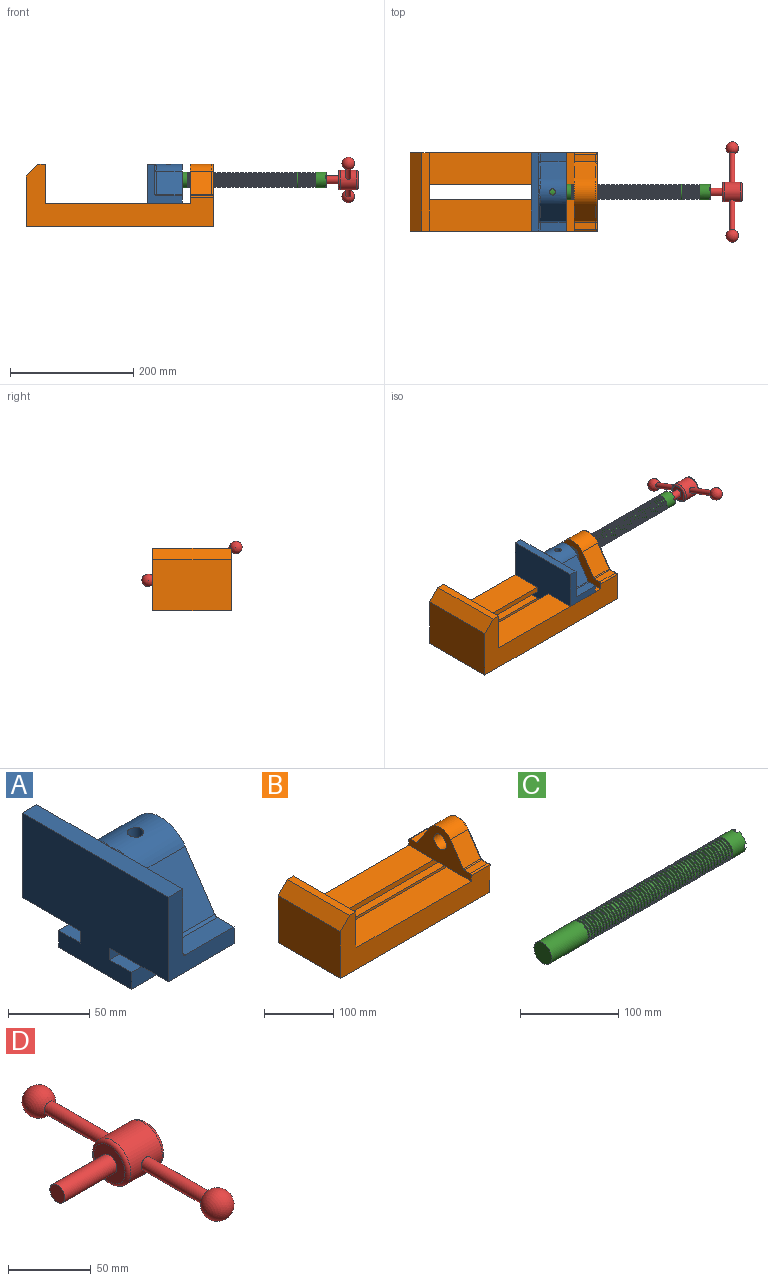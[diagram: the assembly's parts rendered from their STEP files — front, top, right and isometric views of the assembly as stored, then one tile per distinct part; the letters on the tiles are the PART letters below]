
ASSEMBLY  parts=4 mates=3
PART A: 36 faces, bbox 57.2x127x89 mm
  f0: plane 57.15x50.8mm, normal (0,0,-1), area 2903.2mm2, adj f6,f9,f10,f23
  f1: cylinder r=12.7mm len=44.45mm, axis (1,0,0), area 3464.3mm2, adj f6,f15,f16
  f2: plane 41.91x14.52mm, normal (0,0,1), area 608.5mm2, adj f6,f11,f24,f25
  f3: plane 51.86x48.26mm, normal (1,0,0), area 1495.7mm2, adj f8,f10,f31,f33,f35
  f4: plane 51.86x48.26mm, normal (1,0,0), area 1495.7mm2, adj f8,f11,f24,f28,f29
  f5: plane 57.15x50.8mm, normal (0,0,-1), area 2903.2mm2, adj f6,f9,f11,f22
  f6: plane 127x85.09mm, normal (1,0,0), area 5190.6mm2, adj f0,f1,f2,f5,f7,f10,f11,f12
  f7: plane 41.91x14.52mm, normal (0,0,1), area 608.5mm2, adj f6,f10,f30,f31
  f8: plane 127x12.7mm, normal (0,0,1), area 1612.9mm2, adj f3,f4,f9,f10,f11,f26,f34
  f9: plane 127x85.09mm, normal (-1,0,0), area 9096.8mm2, adj f0,f5,f8,f10,f11,f17,f18,f19
  f10: plane 63.5x57.15mm, normal (0,-1,0), area 1372.3mm2, adj f0,f3,f6,f7,f8,f9,f31
  f11: plane 63.5x57.15mm, normal (0,1,0), area 1372.3mm2, adj f2,f4,f5,f6,f8,f9,f24
  f12: plane 41.91x38.43mm, normal (0,-0.83,0.56), area 1939.2mm2, adj f6,f13,f30,f33
  f13: cylinder r=25.4mm len=44.45mm, axis (1,0,0), area 2026.5mm2, adj f6,f12,f14,f16,f26,f28,f34,f35
  f14: plane 41.91x38.43mm, normal (0,0.83,0.56), area 1939.2mm2, adj f6,f13,f25,f29
  f15: plane 25.4x25.4mm, normal (1,0,0), area 506.7mm2, adj f1
  f16: cylinder r=5.08mm len=13.76mm, axis (0,0,1), area 414mm2, adj f1,f13
  f17: plane 57.15x19.05mm, normal (0,0,1), area 1088.7mm2, adj f6,f9,f18,f23
  f18: plane 57.15x12.7mm, normal (0,-1,0), area 725.8mm2, adj f6,f9,f17,f19
  f19: plane 63.5x57.15mm, normal (0,0,-1), area 3629mm2, adj f6,f9,f18,f20
  f20: plane 57.15x12.7mm, normal (0,1,0), area 725.8mm2, adj f6,f9,f19,f21
  f21: plane 57.15x19.05mm, normal (0,0,1), area 1088.7mm2, adj f6,f9,f20,f22
  f22: plane 57.15x8.89mm, normal (0,1,0), area 508.1mm2, adj f5,f6,f9,f21
  f23: plane 57.15x8.89mm, normal (0,-1,0), area 508.1mm2, adj f0,f6,f9,f17
  f24: cylinder r=2.54mm len=14.52mm, axis (0,-1,0), area 57.9mm2, adj f2,f4,f11,f27
  f25: cylinder r=2.54mm len=41.91mm, axis (1,0,0), area 104.3mm2, adj f2,f6,f14,f27
  f26: bspline ~12.24x2.8mm, area 20.9mm2, adj f8,f13,f28
  f27: sphere r=2.54mm, area 6.3mm2, adj f24,f25,f29
  f28: torus R=27.94mm, axis (1,0,0), area 57.8mm2, adj f4,f13,f26,f29
  f29: cylinder r=2.54mm len=39.84mm, axis (0,-0.56,0.83), area 184.6mm2, adj f4,f14,f27,f28
  f30: cylinder r=2.54mm len=41.91mm, axis (1,0,0), area 104.3mm2, adj f6,f7,f12,f32
  f31: cylinder r=2.54mm len=14.52mm, axis (0,-1,0), area 57.9mm2, adj f3,f7,f10,f32
  f32: sphere r=2.54mm, area 6.3mm2, adj f30,f31,f33
  f33: cylinder r=2.54mm len=39.84mm, axis (0,-0.56,-0.83), area 184.6mm2, adj f3,f12,f32,f35
  f34: bspline ~12.24x2.8mm, area 20.9mm2, adj f8,f13,f35
  f35: torus R=27.94mm, axis (1,0,0), area 57.8mm2, adj f3,f13,f33,f34
PART B: 39 faces, bbox 304.8x127x103.7 mm
  f0: plane 234.95x50.8mm, normal (0,0,1), area 11935.5mm2, adj f2,f8,f16,f26
  f1: plane 234.95x50.8mm, normal (0,0,1), area 11935.5mm2, adj f2,f9,f16,f27
  f2: plane 127x101.6mm, normal (1,0,0), area 9516.1mm2, adj f0,f1,f3,f6,f8,f9,f18,f19
  f3: plane 127x12.7mm, normal (0,0,1), area 1612.9mm2, adj f2,f4,f8,f9
  f4: plane 127x19.05mm, normal (-0.71,0,0.71), area 3421.5mm2, adj f3,f5,f8,f9
  f5: plane 127x82.55mm, normal (-1,0,0), area 10483.9mm2, adj f4,f6,f8,f9
  f6: plane 304.8x127mm, normal (0,0,-1), area 31774.1mm2, adj f2,f5,f7,f8,f9,f21,f22
  f7: plane 127x99.06mm, normal (1,0,0), area 7097.5mm2, adj f6,f8,f9,f14,f17,f18,f19,f20
  f8: plane 304.8x101.6mm, normal (0,-1,0), area 13834.6mm2, adj f0,f2,f3,f4,f5,f6,f7,f16
  f9: plane 304.8x101.6mm, normal (0,1,0), area 13834.6mm2, adj f1,f2,f3,f4,f5,f6,f7,f16
  f10: plane 35.56x11.98mm, normal (0,0,1), area 426mm2, adj f16,f28,f29,f30
  f11: plane 38.43x35.56mm, normal (0,0.83,0.56), area 1645.4mm2, adj f12,f16,f29,f32
  f12: cylinder r=25.4mm len=42.19mm, axis (1,0,0), area 1770.2mm2, adj f11,f13,f16,f33
  f13: plane 38.43x35.56mm, normal (0,-0.83,0.56), area 1645.4mm2, adj f12,f16,f34,f35
  f14: cylinder r=12.7mm len=38.1mm, axis (1,0,0), area 3040.2mm2, adj f7,f16
  f15: plane 35.56x11.98mm, normal (0,0,1), area 426mm2, adj f16,f34,f36,f38
  f16: plane 127x63.5mm, normal (-1,0,0), area 4155.5mm2, adj f0,f1,f8,f9,f10,f11,f12,f13
  f17: plane 38.1x25.4mm, normal (0,0,-1), area 967.7mm2, adj f7,f16,f26,f27
  f18: plane 273.05x19.05mm, normal (0,0,-1), area 5201.6mm2, adj f2,f7,f19,f26
  f19: plane 273.05x12.7mm, normal (0,1,0), area 3467.7mm2, adj f2,f7,f18,f20
  f20: plane 273.05x19.05mm, normal (0,0,1), area 5201.6mm2, adj f2,f7,f19,f21
  f21: plane 273.05x16.51mm, normal (0,1,0), area 4508.1mm2, adj f2,f6,f7,f20
  f22: plane 273.05x16.51mm, normal (0,-1,0), area 4508.1mm2, adj f2,f6,f7,f23
  f23: plane 273.05x19.05mm, normal (0,0,1), area 5201.6mm2, adj f2,f7,f22,f24
  f24: plane 273.05x12.7mm, normal (0,-1,0), area 3467.7mm2, adj f2,f7,f23,f25
  f25: plane 273.05x19.05mm, normal (0,0,-1), area 5201.6mm2, adj f2,f7,f24,f27
  f26: plane 273.05x8.89mm, normal (0,1,0), area 2427.4mm2, adj f0,f2,f7,f17,f18
  f27: plane 273.05x8.89mm, normal (0,-1,0), area 2427.4mm2, adj f1,f2,f7,f17,f25
  f28: cylinder r=2.54mm len=38.1mm, axis (1,0,0), area 148.3mm2, adj f9,f10,f16,f30
  f29: cylinder r=2.54mm len=35.56mm, axis (-1,0,0), area 88.5mm2, adj f10,f11,f16,f31
  f30: cylinder r=2.54mm len=14.52mm, axis (0,1,0), area 54.3mm2, adj f7,f10,f28,f31
  f31: torus R=5.08mm, axis (-1,0,0), area 13.5mm2, adj f7,f29,f30,f32
  f32: cylinder r=2.54mm len=39.84mm, axis (0,0.56,-0.83), area 184.6mm2, adj f7,f11,f31,f33
  f33: torus R=22.86mm, axis (-1,0,0), area 191.4mm2, adj f7,f12,f32,f35
  f34: cylinder r=2.54mm len=35.56mm, axis (-1,0,0), area 88.5mm2, adj f13,f15,f16,f37
  f35: cylinder r=2.54mm len=39.84mm, axis (0,0.56,0.83), area 184.6mm2, adj f7,f13,f33,f37
  f36: cylinder r=2.54mm len=38.1mm, axis (-1,0,0), area 148.3mm2, adj f8,f15,f16,f38
  f37: torus R=5.08mm, axis (-1,0,0), area 13.5mm2, adj f7,f34,f35,f38
  f38: cylinder r=2.54mm len=14.52mm, axis (0,1,0), area 54.3mm2, adj f7,f15,f36,f37
PART C: 220 faces, bbox 279.4x25.4x25.4 mm
  f0: cylinder r=12.7mm len=25.4mm, axis (-1,0,0), area 1468.2mm2, adj f1,f2,f3,f5,f7,f208,f209,f210
  f1: plane 9.9x9.9mm, normal (1,0,0), area 62.3mm2, adj f0,f4,f213,f216
  f2: plane 9.9x9.9mm, normal (1,0,0), area 62.3mm2, adj f0,f4,f210,f218
  f3: plane 9.9x9.9mm, normal (1,0,0), area 62.3mm2, adj f0,f4,f209,f212
  f4: cylinder r=6.35mm len=25.4mm, axis (1,0,0), area 960.3mm2, adj f1,f2,f3,f5,f6,f208,f209,f210
  f5: plane 9.9x9.9mm, normal (1,0,0), area 62.3mm2, adj f0,f4,f215,f217
  f6: plane 12.7x12.7mm, normal (1,0,0), area 126.7mm2, adj f4
  f7: cone r=12.7mm half-angle=76deg, axis (1,0,0), area 188mm2, adj f0,f9
  f8: cone r=10.16mm half-angle=76deg, axis (-1,0,0), area 188mm2, adj f9,f10
  f9: cylinder r=10.16mm len=20.32mm, axis (1,0,0), area 81.1mm2, adj f7,f8
  f10: cylinder r=12.7mm len=25.4mm, axis (-1,0,0), area 131.7mm2, adj f8,f11
  f11: cone r=12.7mm half-angle=76deg, axis (1,0,0), area 188mm2, adj f10,f13
  f12: cone r=10.16mm half-angle=76deg, axis (-1,0,0), area 188mm2, adj f13,f14
  f13: cylinder r=10.16mm len=20.32mm, axis (1,0,0), area 81.1mm2, adj f11,f12
  f14: cylinder r=12.7mm len=25.4mm, axis (-1,0,0), area 131.7mm2, adj f12,f15
  f15: cone r=12.7mm half-angle=76deg, axis (1,0,0), area 188mm2, adj f14,f17
  f16: cone r=10.16mm half-angle=76deg, axis (-1,0,0), area 188mm2, adj f17,f18
  f17: cylinder r=10.16mm len=20.32mm, axis (1,0,0), area 81.1mm2, adj f15,f16
  f18: cylinder r=12.7mm len=25.4mm, axis (-1,0,0), area 131.7mm2, adj f16,f19
  f19: cone r=12.7mm half-angle=76deg, axis (1,0,0), area 188mm2, adj f18,f21
  f20: cone r=10.16mm half-angle=76deg, axis (-1,0,0), area 188mm2, adj f21,f22
  f21: cylinder r=10.16mm len=20.32mm, axis (1,0,0), area 81.1mm2, adj f19,f20
  f22: cylinder r=12.7mm len=25.4mm, axis (-1,0,0), area 131.7mm2, adj f20,f23
  f23: cone r=12.7mm half-angle=76deg, axis (1,0,0), area 188mm2, adj f22,f25
  f24: cone r=10.16mm half-angle=76deg, axis (-1,0,0), area 188mm2, adj f25,f26
  f25: cylinder r=10.16mm len=20.32mm, axis (1,0,0), area 81.1mm2, adj f23,f24
  f26: cylinder r=12.7mm len=25.4mm, axis (-1,0,0), area 131.7mm2, adj f24,f27
  f27: cone r=12.7mm half-angle=76deg, axis (1,0,0), area 188mm2, adj f26,f29
  f28: cone r=10.16mm half-angle=76deg, axis (-1,0,0), area 188mm2, adj f29,f30
  f29: cylinder r=10.16mm len=20.32mm, axis (1,0,0), area 81.1mm2, adj f27,f28
  f30: cylinder r=12.7mm len=25.4mm, axis (-1,0,0), area 131.7mm2, adj f28,f31
  f31: cone r=12.7mm half-angle=76deg, axis (1,0,0), area 188mm2, adj f30,f33
  f32: cone r=10.16mm half-angle=76deg, axis (-1,0,0), area 188mm2, adj f33,f34
  f33: cylinder r=10.16mm len=20.32mm, axis (1,0,0), area 81.1mm2, adj f31,f32
  f34: cylinder r=12.7mm len=25.4mm, axis (-1,0,0), area 131.7mm2, adj f32,f35
  f35: cone r=12.7mm half-angle=76deg, axis (1,0,0), area 188mm2, adj f34,f37
  f36: cone r=10.16mm half-angle=76deg, axis (-1,0,0), area 188mm2, adj f37,f38
  f37: cylinder r=10.16mm len=20.32mm, axis (1,0,0), area 81.1mm2, adj f35,f36
  f38: cylinder r=12.7mm len=25.4mm, axis (-1,0,0), area 131.7mm2, adj f36,f39
  f39: cone r=12.7mm half-angle=76deg, axis (1,0,0), area 188mm2, adj f38,f41
  f40: cone r=10.16mm half-angle=76deg, axis (-1,0,0), area 188mm2, adj f41,f42
  f41: cylinder r=10.16mm len=20.32mm, axis (1,0,0), area 81.1mm2, adj f39,f40
  f42: cylinder r=12.7mm len=25.4mm, axis (-1,0,0), area 131.7mm2, adj f40,f43
  f43: cone r=12.7mm half-angle=76deg, axis (1,0,0), area 188mm2, adj f42,f45
  f44: cone r=10.16mm half-angle=76deg, axis (-1,0,0), area 188mm2, adj f45,f46
  f45: cylinder r=10.16mm len=20.32mm, axis (1,0,0), area 81.1mm2, adj f43,f44
  f46: cylinder r=12.7mm len=25.4mm, axis (-1,0,0), area 131.7mm2, adj f44,f47
  f47: cone r=12.7mm half-angle=76deg, axis (1,0,0), area 188mm2, adj f46,f49
  f48: cone r=10.16mm half-angle=76deg, axis (-1,0,0), area 188mm2, adj f49,f50
  f49: cylinder r=10.16mm len=20.32mm, axis (1,0,0), area 81.1mm2, adj f47,f48
  f50: cylinder r=12.7mm len=25.4mm, axis (-1,0,0), area 131.7mm2, adj f48,f51
  f51: cone r=12.7mm half-angle=76deg, axis (1,0,0), area 188mm2, adj f50,f53
  f52: cone r=10.16mm half-angle=76deg, axis (-1,0,0), area 188mm2, adj f53,f54
  f53: cylinder r=10.16mm len=20.32mm, axis (1,0,0), area 81.1mm2, adj f51,f52
  f54: cylinder r=12.7mm len=25.4mm, axis (-1,0,0), area 131.7mm2, adj f52,f55
  f55: cone r=12.7mm half-angle=76deg, axis (1,0,0), area 188mm2, adj f54,f57
  f56: cone r=10.16mm half-angle=76deg, axis (-1,0,0), area 188mm2, adj f57,f58
  f57: cylinder r=10.16mm len=20.32mm, axis (1,0,0), area 81.1mm2, adj f55,f56
  f58: cylinder r=12.7mm len=25.4mm, axis (-1,0,0), area 131.7mm2, adj f56,f59
  f59: cone r=12.7mm half-angle=76deg, axis (1,0,0), area 188mm2, adj f58,f61
  f60: cone r=10.16mm half-angle=76deg, axis (-1,0,0), area 188mm2, adj f61,f62
  f61: cylinder r=10.16mm len=20.32mm, axis (1,0,0), area 81.1mm2, adj f59,f60
  f62: cylinder r=12.7mm len=25.4mm, axis (-1,0,0), area 131.7mm2, adj f60,f63
  f63: cone r=12.7mm half-angle=76deg, axis (1,0,0), area 188mm2, adj f62,f65
  f64: cone r=10.16mm half-angle=76deg, axis (-1,0,0), area 188mm2, adj f65,f66
  f65: cylinder r=10.16mm len=20.32mm, axis (1,0,0), area 81.1mm2, adj f63,f64
  f66: cylinder r=12.7mm len=25.4mm, axis (-1,0,0), area 131.7mm2, adj f64,f67
  f67: cone r=12.7mm half-angle=76deg, axis (1,0,0), area 188mm2, adj f66,f69
  f68: cone r=10.16mm half-angle=76deg, axis (-1,0,0), area 188mm2, adj f69,f70
  f69: cylinder r=10.16mm len=20.32mm, axis (1,0,0), area 81.1mm2, adj f67,f68
  f70: cylinder r=12.7mm len=25.4mm, axis (-1,0,0), area 131.7mm2, adj f68,f71
  f71: cone r=12.7mm half-angle=76deg, axis (1,0,0), area 188mm2, adj f70,f73
  f72: cone r=10.16mm half-angle=76deg, axis (-1,0,0), area 188mm2, adj f73,f74
  f73: cylinder r=10.16mm len=20.32mm, axis (1,0,0), area 81.1mm2, adj f71,f72
  f74: cylinder r=12.7mm len=25.4mm, axis (-1,0,0), area 131.7mm2, adj f72,f75
  f75: cone r=12.7mm half-angle=76deg, axis (1,0,0), area 188mm2, adj f74,f77
  f76: cone r=10.16mm half-angle=76deg, axis (-1,0,0), area 188mm2, adj f77,f78
  f77: cylinder r=10.16mm len=20.32mm, axis (1,0,0), area 81.1mm2, adj f75,f76
  f78: cylinder r=12.7mm len=25.4mm, axis (-1,0,0), area 131.7mm2, adj f76,f79
  f79: cone r=12.7mm half-angle=76deg, axis (1,0,0), area 188mm2, adj f78,f81
  f80: cone r=10.16mm half-angle=76deg, axis (-1,0,0), area 188mm2, adj f81,f82
  f81: cylinder r=10.16mm len=20.32mm, axis (1,0,0), area 81.1mm2, adj f79,f80
  f82: cylinder r=12.7mm len=25.4mm, axis (-1,0,0), area 131.7mm2, adj f80,f83
  f83: cone r=12.7mm half-angle=76deg, axis (1,0,0), area 188mm2, adj f82,f85
  f84: cone r=10.16mm half-angle=76deg, axis (-1,0,0), area 188mm2, adj f85,f86
  f85: cylinder r=10.16mm len=20.32mm, axis (1,0,0), area 81.1mm2, adj f83,f84
  f86: cylinder r=12.7mm len=25.4mm, axis (-1,0,0), area 131.7mm2, adj f84,f87
  f87: cone r=12.7mm half-angle=76deg, axis (1,0,0), area 188mm2, adj f86,f89
  f88: cone r=10.16mm half-angle=76deg, axis (-1,0,0), area 188mm2, adj f89,f90
  f89: cylinder r=10.16mm len=20.32mm, axis (1,0,0), area 81.1mm2, adj f87,f88
  f90: cylinder r=12.7mm len=25.4mm, axis (-1,0,0), area 131.7mm2, adj f88,f91
  f91: cone r=12.7mm half-angle=76deg, axis (1,0,0), area 188mm2, adj f90,f93
  f92: cone r=10.16mm half-angle=76deg, axis (-1,0,0), area 188mm2, adj f93,f94
  f93: cylinder r=10.16mm len=20.32mm, axis (1,0,0), area 81.1mm2, adj f91,f92
  f94: cylinder r=12.7mm len=25.4mm, axis (-1,0,0), area 131.7mm2, adj f92,f95
  f95: cone r=12.7mm half-angle=76deg, axis (1,0,0), area 188mm2, adj f94,f97
  f96: cone r=10.16mm half-angle=76deg, axis (-1,0,0), area 188mm2, adj f97,f98
  f97: cylinder r=10.16mm len=20.32mm, axis (1,0,0), area 81.1mm2, adj f95,f96
  f98: cylinder r=12.7mm len=25.4mm, axis (-1,0,0), area 131.7mm2, adj f96,f99
  f99: cone r=12.7mm half-angle=76deg, axis (1,0,0), area 188mm2, adj f98,f101
  f100: cone r=10.16mm half-angle=76deg, axis (-1,0,0), area 188mm2, adj f101,f102
  f101: cylinder r=10.16mm len=20.32mm, axis (1,0,0), area 81.1mm2, adj f99,f100
  f102: cylinder r=12.7mm len=25.4mm, axis (-1,0,0), area 131.7mm2, adj f100,f103
  f103: cone r=12.7mm half-angle=76deg, axis (1,0,0), area 188mm2, adj f102,f105
  f104: cone r=10.16mm half-angle=76deg, axis (-1,0,0), area 188mm2, adj f105,f106
  f105: cylinder r=10.16mm len=20.32mm, axis (1,0,0), area 81.1mm2, adj f103,f104
  f106: cylinder r=12.7mm len=25.4mm, axis (-1,0,0), area 131.7mm2, adj f104,f107
  f107: cone r=12.7mm half-angle=76deg, axis (1,0,0), area 188mm2, adj f106,f109
  f108: cone r=10.16mm half-angle=76deg, axis (-1,0,0), area 188mm2, adj f109,f110
  f109: cylinder r=10.16mm len=20.32mm, axis (1,0,0), area 81.1mm2, adj f107,f108
  f110: cylinder r=12.7mm len=25.4mm, axis (-1,0,0), area 131.7mm2, adj f108,f111
  f111: cone r=12.7mm half-angle=76deg, axis (1,0,0), area 188mm2, adj f110,f113
  f112: cone r=10.16mm half-angle=76deg, axis (-1,0,0), area 188mm2, adj f113,f114
  f113: cylinder r=10.16mm len=20.32mm, axis (1,0,0), area 81.1mm2, adj f111,f112
  f114: cylinder r=12.7mm len=25.4mm, axis (-1,0,0), area 131.7mm2, adj f112,f115
  f115: cone r=12.7mm half-angle=76deg, axis (1,0,0), area 188mm2, adj f114,f117
  f116: cone r=10.16mm half-angle=76deg, axis (-1,0,0), area 188mm2, adj f117,f118
  f117: cylinder r=10.16mm len=20.32mm, axis (1,0,0), area 81.1mm2, adj f115,f116
  f118: cylinder r=12.7mm len=25.4mm, axis (-1,0,0), area 131.7mm2, adj f116,f119
  f119: cone r=12.7mm half-angle=76deg, axis (1,0,0), area 188mm2, adj f118,f121
  f120: cone r=10.16mm half-angle=76deg, axis (-1,0,0), area 188mm2, adj f121,f122
  f121: cylinder r=10.16mm len=20.32mm, axis (1,0,0), area 81.1mm2, adj f119,f120
  f122: cylinder r=12.7mm len=25.4mm, axis (-1,0,0), area 131.7mm2, adj f120,f123
  f123: cone r=12.7mm half-angle=76deg, axis (1,0,0), area 188mm2, adj f122,f125
  f124: cone r=10.16mm half-angle=76deg, axis (-1,0,0), area 188mm2, adj f125,f126
  f125: cylinder r=10.16mm len=20.32mm, axis (1,0,0), area 81.1mm2, adj f123,f124
  f126: cylinder r=12.7mm len=25.4mm, axis (-1,0,0), area 131.7mm2, adj f124,f127
  f127: cone r=12.7mm half-angle=76deg, axis (1,0,0), area 188mm2, adj f126,f129
  f128: cone r=10.16mm half-angle=76deg, axis (-1,0,0), area 188mm2, adj f129,f130
  f129: cylinder r=10.16mm len=20.32mm, axis (1,0,0), area 81.1mm2, adj f127,f128
  f130: cylinder r=12.7mm len=25.4mm, axis (-1,0,0), area 131.7mm2, adj f128,f131
  f131: cone r=12.7mm half-angle=76deg, axis (1,0,0), area 188mm2, adj f130,f133
  f132: cone r=10.16mm half-angle=76deg, axis (-1,0,0), area 188mm2, adj f133,f134
  f133: cylinder r=10.16mm len=20.32mm, axis (1,0,0), area 81.1mm2, adj f131,f132
  f134: cylinder r=12.7mm len=25.4mm, axis (-1,0,0), area 131.7mm2, adj f132,f135
  f135: cone r=12.7mm half-angle=76deg, axis (1,0,0), area 188mm2, adj f134,f137
  f136: cone r=10.16mm half-angle=76deg, axis (-1,0,0), area 188mm2, adj f137,f138
  f137: cylinder r=10.16mm len=20.32mm, axis (1,0,0), area 81.1mm2, adj f135,f136
  f138: cylinder r=12.7mm len=25.4mm, axis (-1,0,0), area 131.7mm2, adj f136,f139
  f139: cone r=12.7mm half-angle=76deg, axis (1,0,0), area 188mm2, adj f138,f141
  f140: cone r=10.16mm half-angle=76deg, axis (-1,0,0), area 188mm2, adj f141,f142
  f141: cylinder r=10.16mm len=20.32mm, axis (1,0,0), area 81.1mm2, adj f139,f140
  f142: cylinder r=12.7mm len=25.4mm, axis (-1,0,0), area 131.7mm2, adj f140,f143
  f143: cone r=12.7mm half-angle=76deg, axis (1,0,0), area 188mm2, adj f142,f145
  f144: cone r=10.16mm half-angle=76deg, axis (-1,0,0), area 188mm2, adj f145,f146
  f145: cylinder r=10.16mm len=20.32mm, axis (1,0,0), area 81.1mm2, adj f143,f144
  f146: cylinder r=12.7mm len=25.4mm, axis (-1,0,0), area 131.7mm2, adj f144,f147
  f147: cone r=12.7mm half-angle=76deg, axis (1,0,0), area 188mm2, adj f146,f149
  f148: cone r=10.16mm half-angle=76deg, axis (-1,0,0), area 188mm2, adj f149,f150
  f149: cylinder r=10.16mm len=20.32mm, axis (1,0,0), area 81.1mm2, adj f147,f148
  f150: cylinder r=12.7mm len=25.4mm, axis (-1,0,0), area 131.7mm2, adj f148,f151
  f151: cone r=12.7mm half-angle=76deg, axis (1,0,0), area 188mm2, adj f150,f153
  f152: cone r=10.16mm half-angle=76deg, axis (-1,0,0), area 188mm2, adj f153,f154
  f153: cylinder r=10.16mm len=20.32mm, axis (1,0,0), area 81.1mm2, adj f151,f152
  f154: cylinder r=12.7mm len=25.4mm, axis (-1,0,0), area 131.7mm2, adj f152,f155
  f155: cone r=12.7mm half-angle=76deg, axis (1,0,0), area 188mm2, adj f154,f157
  f156: cone r=10.16mm half-angle=76deg, axis (-1,0,0), area 188mm2, adj f157,f158
  f157: cylinder r=10.16mm len=20.32mm, axis (1,0,0), area 81.1mm2, adj f155,f156
  f158: cylinder r=12.7mm len=25.4mm, axis (-1,0,0), area 131.7mm2, adj f156,f159
  f159: cone r=12.7mm half-angle=76deg, axis (1,0,0), area 188mm2, adj f158,f161
  f160: cone r=10.16mm half-angle=76deg, axis (-1,0,0), area 188mm2, adj f161,f162
  f161: cylinder r=10.16mm len=20.32mm, axis (1,0,0), area 81.1mm2, adj f159,f160
  f162: cylinder r=12.7mm len=25.4mm, axis (-1,0,0), area 131.7mm2, adj f160,f163
  f163: cone r=12.7mm half-angle=76deg, axis (1,0,0), area 188mm2, adj f162,f165
  f164: cone r=10.16mm half-angle=76deg, axis (-1,0,0), area 188mm2, adj f165,f166
  f165: cylinder r=10.16mm len=20.32mm, axis (1,0,0), area 81.1mm2, adj f163,f164
  f166: cylinder r=12.7mm len=25.4mm, axis (-1,0,0), area 131.7mm2, adj f164,f167
  f167: cone r=12.7mm half-angle=76deg, axis (1,0,0), area 188mm2, adj f166,f169
  f168: cone r=10.16mm half-angle=76deg, axis (-1,0,0), area 188mm2, adj f169,f170
  f169: cylinder r=10.16mm len=20.32mm, axis (1,0,0), area 81.1mm2, adj f167,f168
  f170: cylinder r=12.7mm len=25.4mm, axis (-1,0,0), area 131.7mm2, adj f168,f171
  f171: cone r=12.7mm half-angle=76deg, axis (1,0,0), area 188mm2, adj f170,f173
  f172: cone r=10.16mm half-angle=76deg, axis (-1,0,0), area 188mm2, adj f173,f174
  f173: cylinder r=10.16mm len=20.32mm, axis (1,0,0), area 81.1mm2, adj f171,f172
  f174: cylinder r=12.7mm len=25.4mm, axis (-1,0,0), area 131.7mm2, adj f172,f175
  f175: cone r=12.7mm half-angle=76deg, axis (1,0,0), area 188mm2, adj f174,f177
  f176: cone r=10.16mm half-angle=76deg, axis (-1,0,0), area 188mm2, adj f177,f178
  f177: cylinder r=10.16mm len=20.32mm, axis (1,0,0), area 81.1mm2, adj f175,f176
  f178: cylinder r=12.7mm len=25.4mm, axis (-1,0,0), area 131.7mm2, adj f176,f179
  f179: cone r=12.7mm half-angle=76deg, axis (1,0,0), area 188mm2, adj f178,f181
  f180: cone r=10.16mm half-angle=76deg, axis (-1,0,0), area 188mm2, adj f181,f182
  f181: cylinder r=10.16mm len=20.32mm, axis (1,0,0), area 81.1mm2, adj f179,f180
  f182: cylinder r=12.7mm len=25.4mm, axis (-1,0,0), area 131.7mm2, adj f180,f183
  f183: cone r=12.7mm half-angle=76deg, axis (1,0,0), area 188mm2, adj f182,f185
  f184: cone r=10.16mm half-angle=76deg, axis (-1,0,0), area 188mm2, adj f185,f186
  f185: cylinder r=10.16mm len=20.32mm, axis (1,0,0), area 81.1mm2, adj f183,f184
  f186: cylinder r=12.7mm len=25.4mm, axis (-1,0,0), area 131.7mm2, adj f184,f187
  f187: cone r=12.7mm half-angle=76deg, axis (1,0,0), area 188mm2, adj f186,f189
  f188: cone r=10.16mm half-angle=76deg, axis (-1,0,0), area 188mm2, adj f189,f190
  f189: cylinder r=10.16mm len=20.32mm, axis (1,0,0), area 81.1mm2, adj f187,f188
  f190: cylinder r=12.7mm len=25.4mm, axis (-1,0,0), area 131.7mm2, adj f188,f191
  f191: cone r=12.7mm half-angle=76deg, axis (1,0,0), area 188mm2, adj f190,f193
  f192: cone r=10.16mm half-angle=76deg, axis (-1,0,0), area 188mm2, adj f193,f194
  f193: cylinder r=10.16mm len=20.32mm, axis (1,0,0), area 81.1mm2, adj f191,f192
  f194: cylinder r=12.7mm len=25.4mm, axis (-1,0,0), area 131.7mm2, adj f192,f195
  f195: cone r=12.7mm half-angle=76deg, axis (1,0,0), area 188mm2, adj f194,f197
  f196: cone r=10.16mm half-angle=76deg, axis (-1,0,0), area 188mm2, adj f197,f198
  f197: cylinder r=10.16mm len=20.32mm, axis (1,0,0), area 81.1mm2, adj f195,f196
  f198: cylinder r=12.7mm len=25.4mm, axis (-1,0,0), area 131.7mm2, adj f196,f199
  f199: cone r=12.7mm half-angle=76deg, axis (1,0,0), area 188mm2, adj f198,f201
  f200: cone r=10.16mm half-angle=76deg, axis (-1,0,0), area 188mm2, adj f201,f202
  f201: cylinder r=10.16mm len=20.32mm, axis (1,0,0), area 81.1mm2, adj f199,f200
  f202: cylinder r=12.7mm len=25.4mm, axis (-1,0,0), area 131.7mm2, adj f200,f203
  f203: cone r=12.7mm half-angle=76deg, axis (1,0,0), area 188mm2, adj f202,f205
  f204: cone r=10.16mm half-angle=76deg, axis (-1,0,0), area 188mm2, adj f205,f207
  f205: cylinder r=10.16mm len=20.32mm, axis (1,0,0), area 81.1mm2, adj f203,f204
  f206: plane 25.4x25.4mm, normal (-1,0,0), area 506.7mm2, adj f207
  f207: cylinder r=12.7mm len=52.45mm, axis (-1,0,0), area 4185.4mm2, adj f204,f206
  f208: plane 6.88x5.08mm, normal (1,0,0), area 32.7mm2, adj f0,f4,f209,f210
  f209: plane 6.62x2.54mm, normal (0,-1,0), area 16.8mm2, adj f0,f3,f4,f208
  f210: plane 6.62x2.54mm, normal (0,1,0), area 16.8mm2, adj f0,f2,f4,f208
  f211: plane 6.88x5.08mm, normal (1,0,0), area 32.7mm2, adj f0,f4,f212,f213
  f212: plane 6.62x2.54mm, normal (0,0,1), area 16.8mm2, adj f0,f3,f4,f211
  f213: plane 6.62x2.54mm, normal (0,0,-1), area 16.8mm2, adj f0,f1,f4,f211
  f214: plane 6.88x5.08mm, normal (1,0,0), area 32.7mm2, adj f0,f4,f215,f216
  f215: plane 6.62x2.54mm, normal (0,1,0), area 16.8mm2, adj f0,f4,f5,f214
  f216: plane 6.62x2.54mm, normal (0,-1,0), area 16.8mm2, adj f0,f1,f4,f214
  f217: plane 6.62x2.54mm, normal (0,0,-1), area 16.8mm2, adj f0,f4,f5,f219
  f218: plane 6.62x2.54mm, normal (0,0,1), area 16.8mm2, adj f0,f2,f4,f219
  f219: plane 6.88x5.08mm, normal (1,0,0), area 32.7mm2, adj f0,f4,f217,f218
PART D: 11 faces, bbox 76.2x172.7x34.4 mm
  f0: sphere r=10.16mm, area 1231.8mm2, adj f1
  f1: cylinder r=4.45mm len=51.82mm, axis (0,1,0), area 1438.5mm2, adj f0,f4
  f2: sphere r=10.16mm, area 1231.8mm2, adj f3
  f3: cylinder r=4.45mm len=51.82mm, axis (0,1,0), area 1438.5mm2, adj f2,f4
  f4: cylinder r=15.88mm len=31.75mm, axis (-1,0,0), area 2534.7mm2, adj f1,f3,f9,f10
  f5: cylinder r=6.35mm len=44.45mm, axis (-1,0,0), area 1773.5mm2, adj f6,f8
  f6: plane 12.7x12.7mm, normal (-1,0,0), area 126.7mm2, adj f5
  f7: plane 26.67x26.67mm, normal (1,0,0), area 558.6mm2, adj f10
  f8: plane 26.67x26.67mm, normal (-1,0,0), area 432mm2, adj f5,f9
  f9: torus R=13.33mm, axis (1,0,0), area 374.8mm2, adj f4,f8
  f10: torus R=13.33mm, axis (1,0,0), area 374.8mm2, adj f4,f7
PLACE A t=(165.1,0,0)mm
PLACE B at identity fixed
PLACE C rot(axis=(-1,0,0),20.5deg) t=(165.1,-26.74,4.85)mm
PLACE D rot(axis=(1,0,0),159.5deg) t=(165.1,26.74,147.55)mm
MATE fastened C.f4 <-> D.f5  axis (1,0,0) through (158.75,0,76.2)mm
MATE slider B.f2 <-> A.f9  axis (-1,0,0) through (-273.05,-63.5,38.1)mm
MATE revolute A.f28 <-> C.f7  axis (1,0,0) through (-95.25,0,76.2)mm
